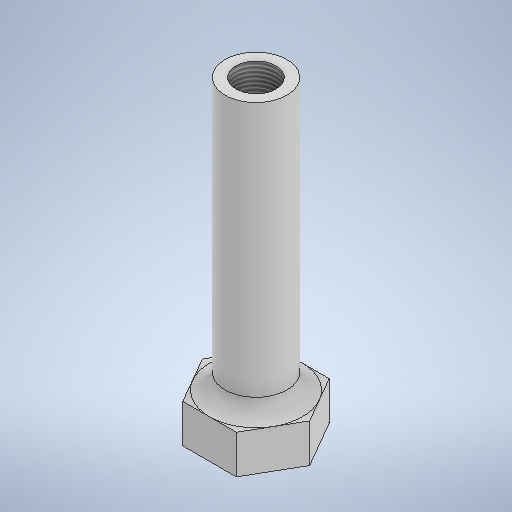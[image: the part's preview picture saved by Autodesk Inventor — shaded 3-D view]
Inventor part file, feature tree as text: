
AUTODESK INVENTOR PART (.ipt)
format: ipt  version: 2025.2 (Build 292293000, 293)  size: 268,800 bytes
history: native  units: mm
features: extrude x3, sketch x3, other x1, thread x1, fillet x1
ambient origin geometry x8: Origin, YZ Plane, XZ Plane, XY Plane, X Axis, Y Axis, Z Axis, Center Point
bodies: Body1 (feature_tree)
feature tree (9):
  other  "Bryła1"
  extrude  "Wyciągnięcie proste1"  Depth=8.0mm
  extrude  "Wyciągnięcie proste2"  Depth=35.0mm TaperAngle=0.0deg
  thread  "Gwint1"
  extrude  "Wyciągnięcie proste3"  Depth=5.2mm
  fillet  "Zaokrąglenie1"  Radius=25.0mm
  sketch  "Szkic1"
  sketch  "Szkic2"
  sketch  "Szkic3"
